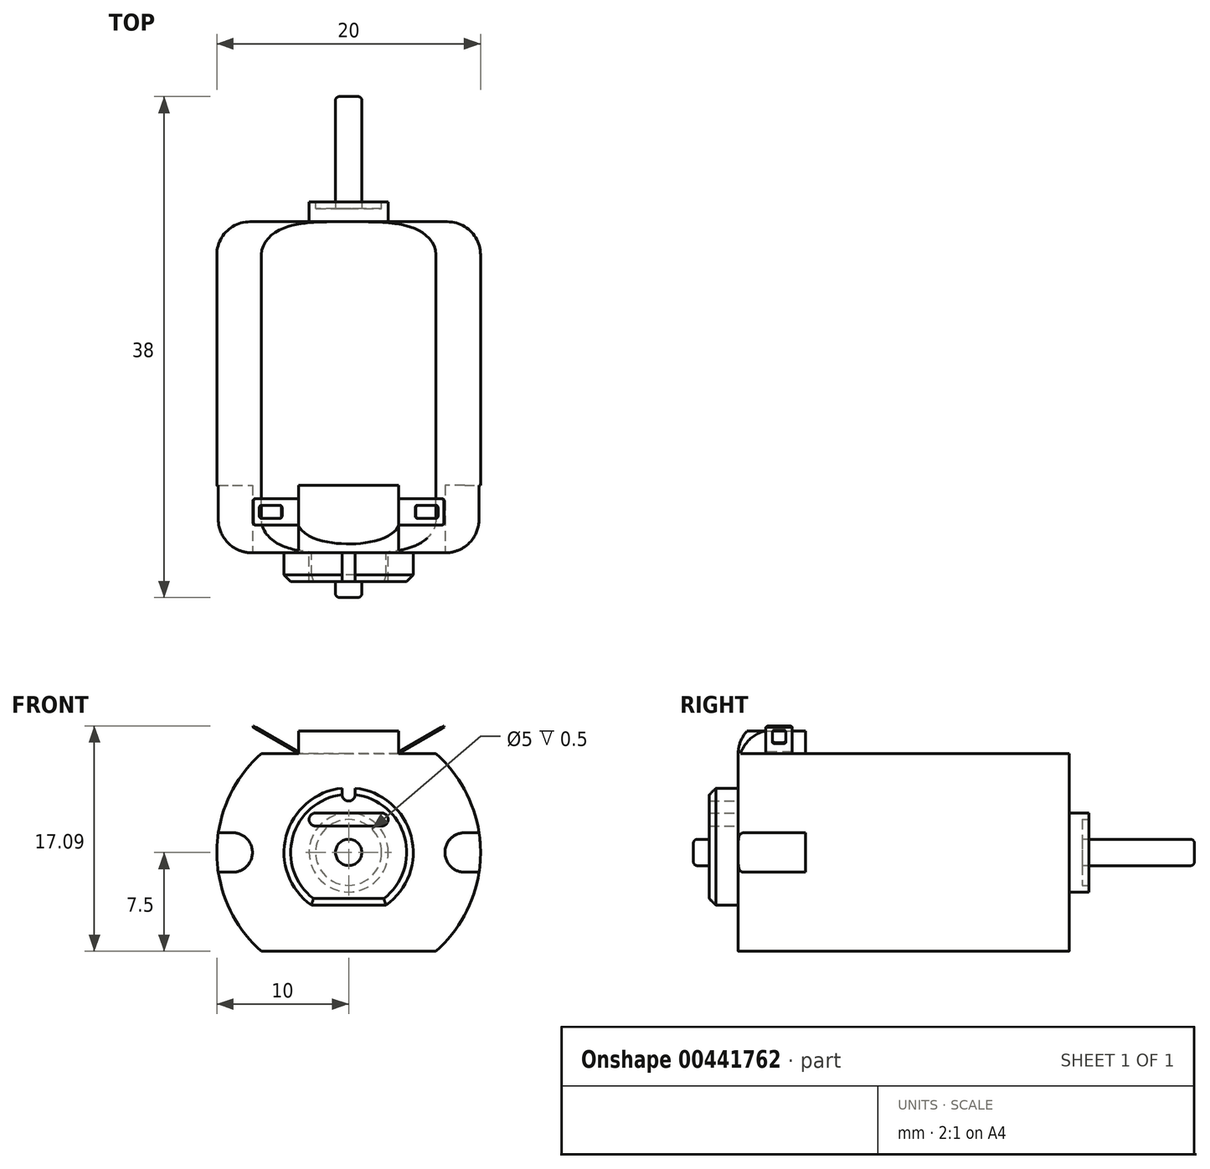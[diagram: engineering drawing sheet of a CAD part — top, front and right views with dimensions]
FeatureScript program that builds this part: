
annotation { "Feature Type Name" : "Feature", "Feature Type Description" : "" }
export const myFeature = defineFeature(function(context is Context, id is Id, definition is map)
    precondition{}
    {
        {
            var Q0;
            Q0=qCreatedBy(makeId("Front.planeOp"),FACE);
            var sketch = newSketch(context, id + "F0", { "sketchPlane" : qUnion([Q0])});
            skCircle(sketch, "E0", {"center": v(0, 0) * mm, "radius": 10 * mm});
            skLineSegment(sketch, "E1", {"start": v(-6.61, 7.5) * mm, "end": v(6.61, 7.5) * mm});
            skLineSegment(sketch, "E2", {"start": v(-6.61, -7.5) * mm, "end": v(6.61, -7.5) * mm});
            skSolve(sketch);
        }
        {
            var Q0;
            {var subQ0=sQuery(id+"F0.wireOp",EDGE,"E1");Q0=makeQuery(id+"F0.imprint","IMPRINT",FACE,{"disambiguationData":[TD([[makeQuery(id+"F0.imprint","IMPRINT",EDGE,{"derivedFrom":subQ0}),-1.0]])]});}
            extrude(context, id + "F1", {"entities" : qUnion([Q0]), "depth" : 25.1 * mm});
        }
        {
            var Q0;
            Q0=makeQuery(id+"F1.opExtrude","CAP_FACE",FACE,{"disambiguationData":[OSD([sQuery(id+"F0.wireOp",EDGE,"E0"),sQuery(id+"F0.wireOp",EDGE,"E1"),sQuery(id+"F0.wireOp",EDGE,"E2")])],"isStart":true});
            var sketch = newSketch(context, id + "F2", { "sketchPlane" : qUnion([Q0])});
            skCircle(sketch, "E3", {"center": v(0, 0) * mm, "radius": 3 * mm});
            skSolve(sketch);
        }
        {
            var Q0;
            Q0 = qSketchRegion(id + "F2", true);
            extrude(context, id + "F3", {"entities" : qUnion([Q0]), "operationType" : NewBodyOperationType.ADD, "depth" : 1.5 * mm});
        }
        {
            var Q0;
            Q0=makeQuery(id+"F3.opExtrude","CAP_FACE",FACE,{"disambiguationData":[OSD([sQuery(id+"F2.wireOp",EDGE,"E3")])],"isStart":false});
            var sketch = newSketch(context, id + "F4", { "sketchPlane" : qUnion([Q0])});
            skCircle(sketch, "E4", {"center": v(0, 0) * mm, "radius": 2.5 * mm});
            skSolve(sketch);
        }
        {
            var Q0;
            Q0 = qSketchRegion(id + "F4", true);
            extrude(context, id + "F5", {"entities" : qUnion([Q0]), "operationType" : NewBodyOperationType.REMOVE, "oppositeDirection" : true, "depth" : 0.5 * mm});
        }
        {
            var Q0;
            Q0=makeQuery(id+"F1.opExtrude","CAP_FACE",FACE,{"disambiguationData":[OSD([sQuery(id+"F0.wireOp",EDGE,"E0"),sQuery(id+"F0.wireOp",EDGE,"E1"),sQuery(id+"F0.wireOp",EDGE,"E2")])],"isStart":true});
            var sketch = newSketch(context, id + "F6", { "sketchPlane" : qUnion([Q0])});
            skCircle(sketch, "E5", {"center": v(0, 0) * mm, "radius": 1 * mm});
            skSolve(sketch);
        }
        {
            var Q0;
            Q0 = qSketchRegion(id + "F6", true);
            extrude(context, id + "F7", {"entities" : qUnion([Q0]), "operationType" : NewBodyOperationType.ADD, "depth" : 9.5 * mm});
        }
        {
            var Q0;
            Q0=makeQuery(id+"F1.opExtrude","CAP_FACE",FACE,{"disambiguationData":[OSD([sQuery(id+"F0.wireOp",EDGE,"E0"),sQuery(id+"F0.wireOp",EDGE,"E1"),sQuery(id+"F0.wireOp",EDGE,"E2")])],"isStart":false});
            var sketch = newSketch(context, id + "F8", { "sketchPlane" : qUnion([Q0])});
            skCircle(sketch, "E6", {"center": v(0, 0) * mm, "radius": 4.9 * mm});
            skLineSegment(sketch, "E7", {"start": v(-2.83, -4) * mm, "end": v(2.83, -4) * mm});
            skLineSegment(sketch, "E8", {"start": v(0.5, 4.4) * mm, "end": v(0.5, 4.87) * mm});
            skLineSegment(sketch, "E9", {"start": v(-0.5, 4.87) * mm, "end": v(-0.5, 4.4) * mm});
            skArc(sketch, "E10", {"start": v(0.5, 4.4) * mm, "mid": v(0, 3.9) * mm, "end": v(-0.5, 4.4) * mm});
            skLineSegment(sketch, "E11.bottom", {"start": v(-2.5, 2) * mm, "end": v(2.5, 2) * mm});
            skLineSegment(sketch, "E11.top", {"start": v(-2.5, 3) * mm, "end": v(2.5, 3) * mm});
            skLineSegment(sketch, "E11.left", {"start": v(-3, 2.5) * mm, "end": v(-3, 2.5) * mm});
            skLineSegment(sketch, "E11.right", {"start": v(3, 2.5) * mm, "end": v(3, 2.5) * mm});
            skPoint(sketch, "E12.visualSharp", {"position": v(-3, 3) * mm});
            skArc(sketch, "E12.filletArc", {"start": v(-2.5, 3) * mm, "mid": v(-2.85, 2.85) * mm, "end": v(-3, 2.5) * mm});
            skPoint(sketch, "E13.visualSharp", {"position": v(-3, 2) * mm});
            skArc(sketch, "E13.filletArc", {"start": v(-3, 2.5) * mm, "mid": v(-2.85, 2.15) * mm, "end": v(-2.5, 2) * mm});
            skPoint(sketch, "E14.visualSharp", {"position": v(3, 2) * mm});
            skArc(sketch, "E14.filletArc", {"start": v(2.5, 2) * mm, "mid": v(2.85, 2.15) * mm, "end": v(3, 2.5) * mm});
            skPoint(sketch, "E15.visualSharp", {"position": v(3, 3) * mm});
            skArc(sketch, "E15.filletArc", {"start": v(3, 2.5) * mm, "mid": v(2.85, 2.85) * mm, "end": v(2.5, 3) * mm});
            skSolve(sketch);
        }
        {
            var Q0;
            {var subQ1=sQuery(id+"F8.wireOp",EDGE,"E7");Q0=makeQuery(id+"F8.imprint","IMPRINT",FACE,{"disambiguationData":[TD([[makeQuery(id+"F8.imprint","IMPRINT",EDGE,{"derivedFrom":subQ1}),1.0]])]});}
            extrude(context, id + "F9", {"entities" : qUnion([Q0]), "operationType" : NewBodyOperationType.ADD, "depth" : 2.2 * mm});
        }
        {
            var Q0;
            Q0=makeQuery(id+"F9.opExtrude","CAP_FACE",FACE,{"disambiguationData":[OSD([sQuery(id+"F8.wireOp",EDGE,"E6"),sQuery(id+"F8.wireOp",EDGE,"E7"),sQuery(id+"F8.wireOp",EDGE,"E8"),sQuery(id+"F8.wireOp",EDGE,"E9"),sQuery(id+"F8.wireOp",EDGE,"E10"),sQuery(id+"F8.wireOp",EDGE,"E11.bottom"),sQuery(id+"F8.wireOp",EDGE,"E11.top"),sQuery(id+"F8.wireOp",EDGE,"E12.filletArc"),sQuery(id+"F8.wireOp",EDGE,"E13.filletArc"),sQuery(id+"F8.wireOp",EDGE,"E14.filletArc"),sQuery(id+"F8.wireOp",EDGE,"E15.filletArc")])],"isStart":false});
            var sketch = newSketch(context, id + "F10", { "sketchPlane" : qUnion([Q0])});
            skCircle(sketch, "E16", {"center": v(0, 0) * mm, "radius": 1 * mm});
            skSolve(sketch);
        }
        {
            var Q0;
            Q0 = qSketchRegion(id + "F10", true);
            extrude(context, id + "F11", {"entities" : qUnion([Q0]), "operationType" : NewBodyOperationType.ADD, "depth" : 1.2 * mm});
        }
        {
            var Q0;
            {var subQ0=sQuery(id+"F0.wireOp",EDGE,"E1");var subQ1=sQuery(id+"F0.wireOp",EDGE,"E0");var subQ2=sQuery(id+"F0.wireOp",EDGE,"E2");Q0=makeQuery(id+"F9.boolean.opBoolean","SPLIT",FACE,{"disambiguationData":[TD([makeQuery(id+"F1.opExtrude","SWEPT_FACE",FACE,{"disambiguationData":[OSD([subQ0])]})])],"derivedFrom":makeQuery(id+"F1.opExtrude","CAP_FACE",FACE,{"disambiguationData":[OSD([subQ1,subQ0,subQ2])],"isStart":false})});}
            var sketch = newSketch(context, id + "F12", { "sketchPlane" : qUnion([Q0])});
            skLineSegment(sketch, "E17", {"start": v(-9.89, 1.5) * mm, "end": v(-8.8, 1.5) * mm});
            skLineSegment(sketch, "E18", {"start": v(-8.8, -1.5) * mm, "end": v(-9.89, -1.5) * mm});
            skArc(sketch, "E19", {"start": v(-8.8, -1.5) * mm, "mid": v(-7.3, 0) * mm, "end": v(-8.8, 1.5) * mm});
            skLineSegment(sketch, "E20", {"start": v(8.8, 1.5) * mm, "end": v(9.89, 1.5) * mm});
            skLineSegment(sketch, "E21", {"start": v(8.8, -1.5) * mm, "end": v(9.89, -1.5) * mm});
            skArc(sketch, "E22", {"start": v(8.8, 1.5) * mm, "mid": v(7.3, 0) * mm, "end": v(8.8, -1.5) * mm});
            skSolve(sketch);
        }
        {
            var Q0;
            Q0=makeQuery(id+"F12.imprint","IMPRINT",FACE,{"disambiguationData":[TD([[makeQuery(id+"F12.imprint","IMPRINT",EDGE,{"derivedFrom":sQuery(id+"F12.wireOp",EDGE,"8CDBdZg8-FexA-tbcI-EJiT-tsh0QVbmtEnx")}),1.0]])]});
            var Q1;
            {var subQ0=sQuery(id+"F12.wireOp",EDGE,"E17");Q1=makeQuery(id+"F12.imprint","IMPRINT",FACE,{"disambiguationData":[TD([[makeQuery(id+"F12.imprint","IMPRINT",EDGE,{"derivedFrom":subQ0}),-1.0]])]});}
            var Q2;
            {var subQ0=sQuery(id+"F12.wireOp",EDGE,"E20");Q2=makeQuery(id+"F12.imprint","IMPRINT",FACE,{"disambiguationData":[TD([[makeQuery(id+"F12.imprint","IMPRINT",EDGE,{"derivedFrom":subQ0}),-1.0]])]});}
            extrude(context, id + "F13", {"entities" : qUnion([Q0, Q1, Q2]), "operationType" : NewBodyOperationType.REMOVE, "oppositeDirection" : true, "depth" : 5.1 * mm});
        }
        {
            var Q0;
            Q0=makeQuery(id+"F1.opExtrude","SWEPT_FACE",FACE,{"disambiguationData":[OSD([sQuery(id+"F0.wireOp",EDGE,"E1")])]});
            var sketch = newSketch(context, id + "F14", { "sketchPlane" : qUnion([Q0])});
            skLineSegment(sketch, "E23.bottom", {"start": v(-3.8, -25.1) * mm, "end": v(3.8, -25.1) * mm});
            skLineSegment(sketch, "E23.top", {"start": v(-3.8, -20) * mm, "end": v(3.8, -20) * mm});
            skLineSegment(sketch, "E23.left", {"start": v(-3.8, -25.1) * mm, "end": v(-3.8, -20) * mm});
            skLineSegment(sketch, "E23.right", {"start": v(3.8, -25.1) * mm, "end": v(3.8, -20) * mm});
            skSolve(sketch);
        }
        {
            var Q0;
            Q0 = qSketchRegion(id + "F14", true);
            extrude(context, id + "F15", {"entities" : qUnion([Q0]), "operationType" : NewBodyOperationType.ADD, "depth" : 1.7 * mm});
        }
        {
            var Q0;
            Q0=qCreatedBy(makeId("Front.planeOp"),FACE);
            cPlane(context, id + "F16", {"entities" : qUnion([Q0]), "cplaneType" : CPlaneType.OFFSET, "offset" : 23 * mm, "width" : 150 * mm, "height" : 150 * mm});
        }
        {
            var Q0;
            Q0=qCreatedBy(id+"F16.planeOp",FACE);
            var sketch = newSketch(context, id + "F17", { "sketchPlane" : qUnion([Q0])});
            skLineSegment(sketch, "E24", {"start": v(3.8, 7.5) * mm, "end": v(7.26, 9.5) * mm});
            skLineSegment(sketch, "E25", {"start": v(7.26, 9.5) * mm, "end": v(7.21, 9.59) * mm});
            skLineSegment(sketch, "E26", {"start": v(7.21, 9.59) * mm, "end": v(3.75, 7.59) * mm});
            skLineSegment(sketch, "E27", {"start": v(3.75, 7.59) * mm, "end": v(3.8, 7.5) * mm});
            skLineSegment(sketch, "E28", {"start": v(-3.8, 7.5) * mm, "end": v(-7.26, 9.5) * mm});
            skLineSegment(sketch, "E29", {"start": v(-7.26, 9.5) * mm, "end": v(-7.21, 9.59) * mm});
            skLineSegment(sketch, "E30", {"start": v(-7.21, 9.59) * mm, "end": v(-3.75, 7.59) * mm});
            skLineSegment(sketch, "E31", {"start": v(-3.75, 7.59) * mm, "end": v(-3.8, 7.5) * mm});
            skSolve(sketch);
        }
        {
            var Q0;
            Q0 = qSketchRegion(id + "F17", true);
            extrude(context, id + "F18", {"entities" : qUnion([Q0]), "operationType" : NewBodyOperationType.ADD, "oppositeDirection" : true, "depth" : 2 * mm});
        }
        {
            var Q0;
            {var subQ1=sQuery(id+"F0.wireOp",EDGE,"E1");var subQ2=sQuery(id+"F0.wireOp",EDGE,"E0");var subQ3=makeQuery(id+"F0.imprint","IMPRINT",EDGE,{"disambiguationData":[TD([[makeQuery(id+"F0.imprint","INTERSECT",VERTEX,{"disambiguationData":[OD(1.0)],"derivedFrom":[subQ2,subQ1]}),1.0]])],"derivedFrom":subQ2});Q0=makeQuery(id+"F13.boolean.opBoolean","SPLIT",EDGE,{"disambiguationData":[TD([makeQuery(id+"F1.opExtrude","SWEPT_FACE",FACE,{"disambiguationData":[OSD([subQ1])]})])],"derivedFrom":makeQuery(id+"F1.opExtrude","CAP_EDGE",EDGE,{"disambiguationData":[OSD([subQ2]),TDD([subQ3])],"isStart":false})});}
            var Q1;
            {var subQ0=sQuery(id+"F0.wireOp",EDGE,"E2");var subQ1=sQuery(id+"F0.wireOp",EDGE,"E1");var subQ2=sQuery(id+"F0.wireOp",EDGE,"E0");var subQ3=makeQuery(id+"F0.imprint","IMPRINT",EDGE,{"disambiguationData":[TD([[makeQuery(id+"F0.imprint","INTERSECT",VERTEX,{"disambiguationData":[OD(1.0)],"derivedFrom":[subQ2,subQ1]}),1.0]])],"derivedFrom":subQ2});Q1=makeQuery(id+"F13.boolean.opBoolean","SPLIT",EDGE,{"disambiguationData":[TD([makeQuery(id+"F1.opExtrude","SWEPT_FACE",FACE,{"disambiguationData":[OSD([subQ0])]})])],"derivedFrom":makeQuery(id+"F1.opExtrude","CAP_EDGE",EDGE,{"disambiguationData":[OSD([subQ2]),TDD([subQ3])],"isStart":false})});}
            var Q2;
            {var subQ0=sQuery(id+"F0.wireOp",EDGE,"E1");var subQ1=sQuery(id+"F0.wireOp",EDGE,"E0");var subQ2=sQuery(id+"F0.wireOp",EDGE,"E2");var subQ3=makeQuery(id+"F0.imprint","IMPRINT",EDGE,{"disambiguationData":[TD([[makeQuery(id+"F0.imprint","INTERSECT",VERTEX,{"disambiguationData":[OD(0.0)],"derivedFrom":[subQ1,subQ0]}),-1.0]])],"derivedFrom":subQ1});Q2=makeQuery(id+"F13.boolean.opBoolean","SPLIT",EDGE,{"disambiguationData":[TD([makeQuery(id+"F1.opExtrude","SWEPT_FACE",FACE,{"disambiguationData":[OSD([subQ2])]})])],"derivedFrom":makeQuery(id+"F1.opExtrude","CAP_EDGE",EDGE,{"disambiguationData":[OSD([subQ1]),TDD([subQ3])],"isStart":false})});}
            var Q3;
            {var subQ0=sQuery(id+"F0.wireOp",EDGE,"E0");Q3=makeQuery(id+"F1.opExtrude","CAP_EDGE",EDGE,{"disambiguationData":[OSD([subQ0]),TDD([makeQuery(id+"F0.imprint","IMPRINT",EDGE,{"disambiguationData":[TD([[makeQuery(id+"F0.imprint","INTERSECT",VERTEX,{"disambiguationData":[OD(1.0)],"derivedFrom":[subQ0,sQuery(id+"F0.wireOp",EDGE,"E1")]}),1.0]])],"derivedFrom":subQ0})])],"isStart":true});}
            var Q4;
            {var subQ0=sQuery(id+"F0.wireOp",EDGE,"E0");Q4=makeQuery(id+"F1.opExtrude","CAP_EDGE",EDGE,{"disambiguationData":[OSD([subQ0]),TDD([makeQuery(id+"F0.imprint","IMPRINT",EDGE,{"disambiguationData":[TD([[makeQuery(id+"F0.imprint","INTERSECT",VERTEX,{"disambiguationData":[OD(0.0)],"derivedFrom":[subQ0,sQuery(id+"F0.wireOp",EDGE,"E1")]}),-1.0]])],"derivedFrom":subQ0})])],"isStart":true});}
            fillet(context, id + "F19", {"entities" : qUnion([Q0, Q1, Q2, Q3, Q4]), "radius" : 2.5 * mm, "tangentPropagation" : true, "allowEdgeOverflow" : false});
        }
        {
            var Q0;
            {var subQ0=sQuery(id+"F8.wireOp",EDGE,"E6");Q0=makeQuery(id+"F9.opExtrude","CAP_EDGE",EDGE,{"disambiguationData":[OSD([subQ0]),TDD([makeQuery(id+"F8.imprint","IMPRINT",EDGE,{"disambiguationData":[TD([[makeQuery(id+"F8.imprint","INTERSECT",VERTEX,{"disambiguationData":[OD(1.0)],"derivedFrom":[subQ0,sQuery(id+"F8.wireOp",EDGE,"E7")]}),-1.0]])],"derivedFrom":subQ0})])],"isStart":false});}
            var Q1;
            Q1=makeQuery(id+"F9.opExtrude","CAP_EDGE",EDGE,{"disambiguationData":[OSD([sQuery(id+"F8.wireOp",EDGE,"E7")])],"isStart":false});
            var Q2;
            {var subQ0=sQuery(id+"F8.wireOp",EDGE,"E6");Q2=makeQuery(id+"F9.opExtrude","CAP_EDGE",EDGE,{"disambiguationData":[OSD([subQ0]),TDD([makeQuery(id+"F8.imprint","IMPRINT",EDGE,{"disambiguationData":[TD([[makeQuery(id+"F8.imprint","INTERSECT",VERTEX,{"disambiguationData":[OD(0.0)],"derivedFrom":[subQ0,sQuery(id+"F8.wireOp",EDGE,"E7")]}),1.0]])],"derivedFrom":subQ0})])],"isStart":false});}
            chamfer(context, id + "F20", {"entities" : qUnion([Q0, Q1, Q2]), "width" : 0.5 * mm, "tangentPropagation" : true});
        }
        {
            var Q0;
            Q0=makeQuery(id+"F7.opExtrude","CAP_EDGE",EDGE,{"disambiguationData":[OSD([sQuery(id+"F6.wireOp",EDGE,"E5")])],"isStart":false});
            var Q1;
            Q1=makeQuery(id+"F11.opExtrude","CAP_EDGE",EDGE,{"disambiguationData":[OSD([sQuery(id+"F10.wireOp",EDGE,"E16")])],"isStart":false});
            fillet(context, id + "F21", {"entities" : qUnion([Q0, Q1]), "radius" : 0.3 * mm, "tangentPropagation" : true, "allowEdgeOverflow" : false});
        }
        {
            var Q0;
            Q0=makeQuery(id+"F18.opExtrude","SWEPT_FACE",FACE,{"disambiguationData":[OSD([sQuery(id+"F17.wireOp",EDGE,"E26")])]});
            var sketch = newSketch(context, id + "F22", { "sketchPlane" : qUnion([Q0])});
            skLineSegment(sketch, "E32.bottom", {"start": v(8.74, -21.5) * mm, "end": v(10.34, -21.5) * mm});
            skLineSegment(sketch, "E32.top", {"start": v(8.74, -22.5) * mm, "end": v(10.34, -22.5) * mm});
            skLineSegment(sketch, "E32.left", {"start": v(8.54, -21.7) * mm, "end": v(8.54, -22.3) * mm});
            skLineSegment(sketch, "E32.right", {"start": v(10.54, -21.7) * mm, "end": v(10.54, -22.3) * mm});
            skPoint(sketch, "E33.visualSharp", {"position": v(8.54, -21.5) * mm});
            skArc(sketch, "E33.filletArc", {"start": v(8.74, -21.5) * mm, "mid": v(8.6, -21.56) * mm, "end": v(8.54, -21.7) * mm});
            skPoint(sketch, "E34.visualSharp", {"position": v(8.54, -22.5) * mm});
            skArc(sketch, "E34.filletArc", {"start": v(8.54, -22.3) * mm, "mid": v(8.6, -22.44) * mm, "end": v(8.74, -22.5) * mm});
            skPoint(sketch, "E35.visualSharp", {"position": v(10.54, -22.5) * mm});
            skArc(sketch, "E35.filletArc", {"start": v(10.34, -22.5) * mm, "mid": v(10.48, -22.44) * mm, "end": v(10.54, -22.3) * mm});
            skPoint(sketch, "E36.visualSharp", {"position": v(10.54, -21.5) * mm});
            skArc(sketch, "E36.filletArc", {"start": v(10.54, -21.7) * mm, "mid": v(10.48, -21.56) * mm, "end": v(10.34, -21.5) * mm});
            skSolve(sketch);
        }
        {
            var Q0;
            Q0 = qSketchRegion(id + "F22", true);
            extrude(context, id + "F23", {"entities" : qUnion([Q0]), "operationType" : NewBodyOperationType.REMOVE, "oppositeDirection" : true, "depth" : 0.1 * mm});
        }
        {
            var Q0;
            Q0=makeQuery(id+"F18.opExtrude","SWEPT_FACE",FACE,{"disambiguationData":[OSD([sQuery(id+"F17.wireOp",EDGE,"E30")])]});
            var sketch = newSketch(context, id + "F24", { "sketchPlane" : qUnion([Q0])});
            skLineSegment(sketch, "E37.bottom", {"start": v(-10.34, -21.5) * mm, "end": v(-8.74, -21.5) * mm});
            skLineSegment(sketch, "E37.top", {"start": v(-10.34, -22.5) * mm, "end": v(-8.74, -22.5) * mm});
            skLineSegment(sketch, "E37.left", {"start": v(-10.54, -21.7) * mm, "end": v(-10.54, -22.3) * mm});
            skLineSegment(sketch, "E37.right", {"start": v(-8.54, -21.7) * mm, "end": v(-8.54, -22.3) * mm});
            skPoint(sketch, "E38.visualSharp", {"position": v(-10.54, -21.5) * mm});
            skArc(sketch, "E38.filletArc", {"start": v(-10.34, -21.5) * mm, "mid": v(-10.48, -21.56) * mm, "end": v(-10.54, -21.7) * mm});
            skPoint(sketch, "E39.visualSharp", {"position": v(-8.54, -21.5) * mm});
            skArc(sketch, "E39.filletArc", {"start": v(-8.54, -21.7) * mm, "mid": v(-8.6, -21.56) * mm, "end": v(-8.74, -21.5) * mm});
            skPoint(sketch, "E40.visualSharp", {"position": v(-8.54, -22.5) * mm});
            skArc(sketch, "E40.filletArc", {"start": v(-8.74, -22.5) * mm, "mid": v(-8.6, -22.44) * mm, "end": v(-8.54, -22.3) * mm});
            skPoint(sketch, "E41.visualSharp", {"position": v(-10.54, -22.5) * mm});
            skArc(sketch, "E41.filletArc", {"start": v(-10.54, -22.3) * mm, "mid": v(-10.48, -22.44) * mm, "end": v(-10.34, -22.5) * mm});
            skSolve(sketch);
        }
        {
            var Q0;
            Q0 = qSketchRegion(id + "F24", true);
            extrude(context, id + "F25", {"entities" : qUnion([Q0]), "operationType" : NewBodyOperationType.REMOVE, "oppositeDirection" : true, "depth" : 0.1 * mm});
        }
        {
            var Q0;
            Q0=makeQuery(id+"F18.opExtrude","CAP_EDGE",EDGE,{"disambiguationData":[OSD([sQuery(id+"F17.wireOp",EDGE,"E25")])],"isStart":false});
            var Q1;
            Q1=makeQuery(id+"F18.opExtrude","CAP_EDGE",EDGE,{"disambiguationData":[OSD([sQuery(id+"F17.wireOp",EDGE,"E25")])],"isStart":true});
            var Q2;
            Q2=makeQuery(id+"F18.opExtrude","CAP_EDGE",EDGE,{"disambiguationData":[OSD([sQuery(id+"F17.wireOp",EDGE,"E29")])],"isStart":false});
            var Q3;
            Q3=makeQuery(id+"F18.opExtrude","CAP_EDGE",EDGE,{"disambiguationData":[OSD([sQuery(id+"F17.wireOp",EDGE,"E29")])],"isStart":true});
            fillet(context, id + "F26", {"entities" : qUnion([Q0, Q1, Q2, Q3]), "radius" : 0.2 * mm, "tangentPropagation" : true, "allowEdgeOverflow" : false});
        }
    });
